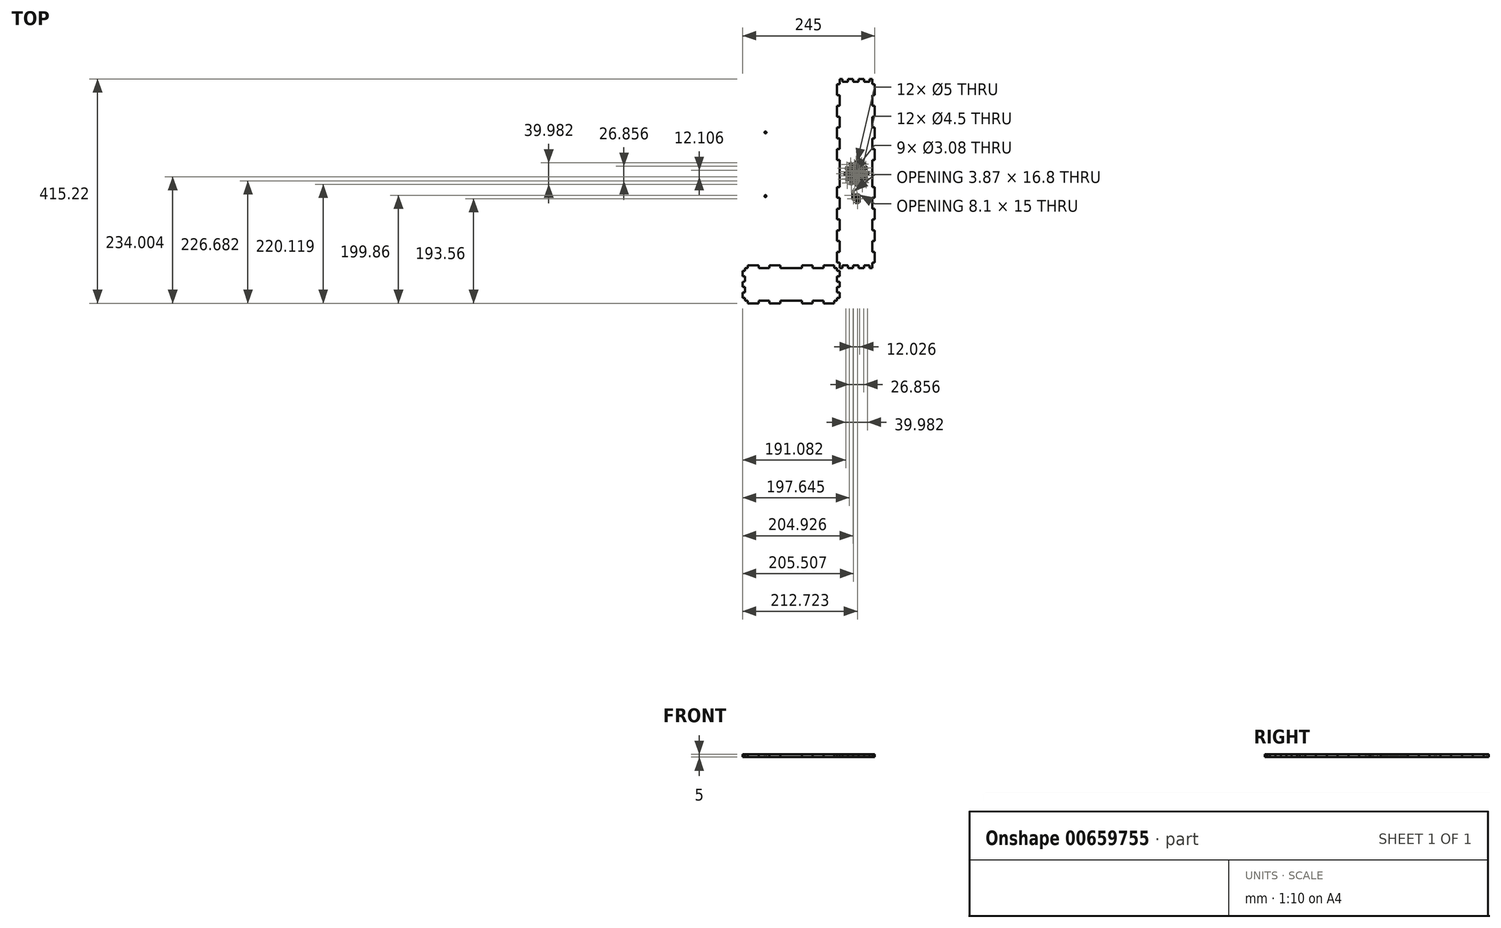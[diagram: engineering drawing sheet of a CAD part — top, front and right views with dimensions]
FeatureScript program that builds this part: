
annotation { "Feature Type Name" : "Feature", "Feature Type Description" : "" }
export const myFeature = defineFeature(function(context is Context, id is Id, definition is map)
    precondition{}
    {
        {
            assignVariable(context, id + "F0", {"name" : "thickness", "anyValue" : 5});
        }
        {
            var Q0;
            Q0=qCreatedBy(makeId("Top.planeOp"),FACE);
            var sketch = newSketch(context, id + "F1", { "sketchPlane" : qUnion([Q0])});
            skLineSegment(sketch, "E0", {"start": v(-90, 175.1) * mm, "end": v(-90, 165.1) * mm});
            skLineSegment(sketch, "E1", {"start": v(-80, 175.1) * mm, "end": v(-90, 175.1) * mm});
            skLineSegment(sketch, "E2", {"start": v(-80, 175.1) * mm, "end": v(-80, 170.1) * mm});
            skLineSegment(sketch, "E3", {"start": v(-80, 170.1) * mm, "end": v(-60, 170.1) * mm});
            skLineSegment(sketch, "E4", {"start": v(-60, 170.1) * mm, "end": v(-60, 175.1) * mm});
            skLineSegment(sketch, "E5.direction1", {"start": v(-80, 170.1) * mm, "end": v(-40, 170.1) * mm, "construction": true});
            skLineSegment(sketch, "E6", {"start": v(-90, 165.1) * mm, "end": v(-85, 165.1) * mm});
            skLineSegment(sketch, "E7", {"start": v(-85, 165.1) * mm, "end": v(-85, 145.1) * mm});
            skLineSegment(sketch, "E8", {"start": v(-85, 145.1) * mm, "end": v(-90, 145.1) * mm});
            skLineSegment(sketch, "E9.0.1.0", {"start": v(-90, 125.1) * mm, "end": v(-85, 125.1) * mm});
            skLineSegment(sketch, "E9.0.1.1", {"start": v(-85, 125.1) * mm, "end": v(-85, 105.1) * mm});
            skLineSegment(sketch, "E9.0.1.2", {"start": v(-85, 105.1) * mm, "end": v(-90, 105.1) * mm});
            skLineSegment(sketch, "E9.0.2.0", {"start": v(-90, 85.1) * mm, "end": v(-85, 85.1) * mm});
            skLineSegment(sketch, "E9.0.2.1", {"start": v(-85, 85.1) * mm, "end": v(-85, 65.1) * mm});
            skLineSegment(sketch, "E9.0.2.2", {"start": v(-85, 65.1) * mm, "end": v(-90, 65.1) * mm});
            skLineSegment(sketch, "E9.0.3.0", {"start": v(-90, 45.1) * mm, "end": v(-85, 45.1) * mm});
            skLineSegment(sketch, "E9.0.3.1", {"start": v(-85, 45.1) * mm, "end": v(-85, 25.1) * mm});
            skLineSegment(sketch, "E9.0.3.2", {"start": v(-85, 25.1) * mm, "end": v(-90, 25.1) * mm});
            skLineSegment(sketch, "E9.direction1", {"start": v(-90, 165.1) * mm, "end": v(-88.53, 165.1) * mm, "construction": true});
            skLineSegment(sketch, "E9.direction2", {"start": v(-90, 165.1) * mm, "end": v(-90, 125.1) * mm, "construction": true});
            skLineSegment(sketch, "E10.0.1.0", {"start": v(-40, 175.1) * mm, "end": v(-40, 170.1) * mm});
            skLineSegment(sketch, "E10.3.1.0", {"start": v(-40, 170.1) * mm, "end": v(-20, 170.1) * mm});
            skLineSegment(sketch, "E10.6.1.0", {"start": v(-20, 170.1) * mm, "end": v(-20, 175.1) * mm});
            skLineSegment(sketch, "E11", {"start": v(-60, 175.1) * mm, "end": v(-40, 175.1) * mm});
            skLineSegment(sketch, "E12", {"start": v(-20, 175.1) * mm, "end": v(0, 175.1) * mm});
            skLineSegment(sketch, "E13", {"start": v(-90, 145.1) * mm, "end": v(-90, 125.1) * mm});
            skLineSegment(sketch, "E14", {"start": v(-90, 105.1) * mm, "end": v(-90, 85.1) * mm});
            skLineSegment(sketch, "E15", {"start": v(-90, 65.1) * mm, "end": v(-90, 45.1) * mm});
            skLineSegment(sketch, "E16", {"start": v(-90, 25.1) * mm, "end": v(-90, 0) * mm});
            skLineSegment(sketch, "E17.MirrorCS", {"start": v(20, 175.1) * mm, "end": v(0, 175.1) * mm});
            skLineSegment(sketch, "E18.MirrorCS", {"start": v(20, 170.1) * mm, "end": v(20, 175.1) * mm});
            skLineSegment(sketch, "E19.MirrorCS", {"start": v(40, 170.1) * mm, "end": v(20, 170.1) * mm});
            skLineSegment(sketch, "E20.MirrorCS", {"start": v(40, 175.1) * mm, "end": v(40, 170.1) * mm});
            skLineSegment(sketch, "E21.MirrorCS", {"start": v(60, 175.1) * mm, "end": v(40, 175.1) * mm});
            skLineSegment(sketch, "E22.MirrorCS", {"start": v(60, 170.1) * mm, "end": v(60, 175.1) * mm});
            skLineSegment(sketch, "E23.MirrorCS", {"start": v(80, 170.1) * mm, "end": v(40, 170.1) * mm, "construction": true});
            skLineSegment(sketch, "E24.MirrorCS", {"start": v(80, 175.1) * mm, "end": v(80, 170.1) * mm});
            skLineSegment(sketch, "E25.MirrorCS", {"start": v(80, 175.1) * mm, "end": v(90, 175.1) * mm});
            skLineSegment(sketch, "E26.MirrorCS", {"start": v(90, 175.1) * mm, "end": v(90, 165.1) * mm});
            skLineSegment(sketch, "E27.MirrorCS", {"start": v(90, 165.1) * mm, "end": v(88.53, 165.1) * mm, "construction": true});
            skLineSegment(sketch, "E28.MirrorCS", {"start": v(85, 165.1) * mm, "end": v(85, 145.1) * mm});
            skLineSegment(sketch, "E29.MirrorCS", {"start": v(85, 145.1) * mm, "end": v(90, 145.1) * mm});
            skLineSegment(sketch, "E30.MirrorCS", {"start": v(90, 165.1) * mm, "end": v(90, 125.1) * mm, "construction": true});
            skLineSegment(sketch, "E31.MirrorCS", {"start": v(85, 125.1) * mm, "end": v(85, 105.1) * mm});
            skLineSegment(sketch, "E32.MirrorCS", {"start": v(90, 125.1) * mm, "end": v(85, 125.1) * mm});
            skLineSegment(sketch, "E33.MirrorCS", {"start": v(85, 105.1) * mm, "end": v(90, 105.1) * mm});
            skLineSegment(sketch, "E34.MirrorCS", {"start": v(85, 85.1) * mm, "end": v(85, 65.1) * mm});
            skLineSegment(sketch, "E35.MirrorCS", {"start": v(90, 105.1) * mm, "end": v(90, 85.1) * mm});
            skLineSegment(sketch, "E36.MirrorCS", {"start": v(90, 85.1) * mm, "end": v(85, 85.1) * mm});
            skLineSegment(sketch, "E37.MirrorCS", {"start": v(85, 65.1) * mm, "end": v(90, 65.1) * mm});
            skLineSegment(sketch, "E38.MirrorCS", {"start": v(90, 65.1) * mm, "end": v(90, 45.1) * mm});
            skLineSegment(sketch, "E39.MirrorCS", {"start": v(90, 45.1) * mm, "end": v(85, 45.1) * mm});
            skLineSegment(sketch, "E40.MirrorCS", {"start": v(85, 45.1) * mm, "end": v(85, 25.1) * mm});
            skLineSegment(sketch, "E41.MirrorCS", {"start": v(85, 25.1) * mm, "end": v(90, 25.1) * mm});
            skLineSegment(sketch, "E42.MirrorCS", {"start": v(90, 25.1) * mm, "end": v(90, 0) * mm});
            skLineSegment(sketch, "E43.MirrorCS", {"start": v(90, 165.1) * mm, "end": v(85, 165.1) * mm});
            skLineSegment(sketch, "E44.MirrorCS", {"start": v(90, 145.1) * mm, "end": v(90, 125.1) * mm});
            skLineSegment(sketch, "E45.MirrorCS", {"start": v(90, -165.1) * mm, "end": v(88.53, -165.1) * mm, "construction": true});
            skLineSegment(sketch, "E46.MirrorCS", {"start": v(90, -125.1) * mm, "end": v(85, -125.1) * mm});
            skLineSegment(sketch, "E47.MirrorCS", {"start": v(60, -170.1) * mm, "end": v(60, -175.1) * mm});
            skLineSegment(sketch, "E48.MirrorCS", {"start": v(90, -85.1) * mm, "end": v(85, -85.1) * mm});
            skLineSegment(sketch, "E49.MirrorCS", {"start": v(90, -175.1) * mm, "end": v(90, -165.1) * mm});
            skLineSegment(sketch, "E50.MirrorCS", {"start": v(85, -105.1) * mm, "end": v(90, -105.1) * mm});
            skLineSegment(sketch, "E51.MirrorCS", {"start": v(85, -145.1) * mm, "end": v(90, -145.1) * mm});
            skLineSegment(sketch, "E52.MirrorCS", {"start": v(85, -65.1) * mm, "end": v(90, -65.1) * mm});
            skLineSegment(sketch, "E53.MirrorCS", {"start": v(40, -175.1) * mm, "end": v(40, -170.1) * mm});
            skLineSegment(sketch, "E54.MirrorCS", {"start": v(80, -175.1) * mm, "end": v(80, -170.1) * mm});
            skLineSegment(sketch, "E55.MirrorCS", {"start": v(90, -145.1) * mm, "end": v(90, -125.1) * mm});
            skLineSegment(sketch, "E56.MirrorCS", {"start": v(20, -170.1) * mm, "end": v(20, -175.1) * mm});
            skLineSegment(sketch, "E57.MirrorCS", {"start": v(90, -45.1) * mm, "end": v(85, -45.1) * mm});
            skLineSegment(sketch, "E58.MirrorCS", {"start": v(90, -165.1) * mm, "end": v(85, -165.1) * mm});
            skLineSegment(sketch, "E59.MirrorCS", {"start": v(85, -25.1) * mm, "end": v(90, -25.1) * mm});
            skLineSegment(sketch, "E60.MirrorCS", {"start": v(90, -165.1) * mm, "end": v(90, -125.1) * mm, "construction": true});
            skLineSegment(sketch, "E61.MirrorCS", {"start": v(85, -125.1) * mm, "end": v(85, -105.1) * mm});
            skLineSegment(sketch, "E62.MirrorCS", {"start": v(40, -170.1) * mm, "end": v(20, -170.1) * mm});
            skLineSegment(sketch, "E63.MirrorCS", {"start": v(85, -45.1) * mm, "end": v(85, -25.1) * mm});
            skLineSegment(sketch, "E64.MirrorCS", {"start": v(80, -170.1) * mm, "end": v(40, -170.1) * mm, "construction": true});
            skLineSegment(sketch, "E65.MirrorCS", {"start": v(85, -85.1) * mm, "end": v(85, -65.1) * mm});
            skLineSegment(sketch, "E66.MirrorCS", {"start": v(20, -175.1) * mm, "end": v(0, -175.1) * mm});
            skLineSegment(sketch, "E67.MirrorCS", {"start": v(90, -65.1) * mm, "end": v(90, -45.1) * mm});
            skLineSegment(sketch, "E68.MirrorCS", {"start": v(80, -175.1) * mm, "end": v(85, -175.1) * mm});
            skLineSegment(sketch, "E69.MirrorCS", {"start": v(90, -105.1) * mm, "end": v(90, -85.1) * mm});
            skLineSegment(sketch, "E70.MirrorCS", {"start": v(90, -25.1) * mm, "end": v(90, 0) * mm});
            skLineSegment(sketch, "E71.MirrorCS", {"start": v(85, -165.1) * mm, "end": v(85, -145.1) * mm});
            skLineSegment(sketch, "E72.MirrorCS", {"start": v(60, -175.1) * mm, "end": v(40, -175.1) * mm});
            skLineSegment(sketch, "E73.MirrorCS", {"start": v(-90, -165.1) * mm, "end": v(-88.53, -165.1) * mm, "construction": true});
            skLineSegment(sketch, "E74.MirrorCS", {"start": v(-90, -165.1) * mm, "end": v(-85, -165.1) * mm});
            skLineSegment(sketch, "E75.MirrorCS", {"start": v(-90, -125.1) * mm, "end": v(-85, -125.1) * mm});
            skLineSegment(sketch, "E76.MirrorCS", {"start": v(-85, -105.1) * mm, "end": v(-90, -105.1) * mm});
            skLineSegment(sketch, "E77.MirrorCS", {"start": v(-40, -175.1) * mm, "end": v(-40, -170.1) * mm});
            skLineSegment(sketch, "E78.MirrorCS", {"start": v(-60, -170.1) * mm, "end": v(-60, -175.1) * mm});
            skLineSegment(sketch, "E79.MirrorCS", {"start": v(-85, -145.1) * mm, "end": v(-90, -145.1) * mm});
            skLineSegment(sketch, "E80.MirrorCS", {"start": v(-80, -175.1) * mm, "end": v(-80, -170.1) * mm});
            skLineSegment(sketch, "E81.MirrorCS", {"start": v(-85, -25.1) * mm, "end": v(-90, -25.1) * mm});
            skLineSegment(sketch, "E82.MirrorCS", {"start": v(-90, -45.1) * mm, "end": v(-85, -45.1) * mm});
            skLineSegment(sketch, "E83.MirrorCS", {"start": v(-90, -145.1) * mm, "end": v(-90, -125.1) * mm});
            skLineSegment(sketch, "E84.MirrorCS", {"start": v(-90, -85.1) * mm, "end": v(-85, -85.1) * mm});
            skLineSegment(sketch, "E85.MirrorCS", {"start": v(-20, -170.1) * mm, "end": v(-20, -175.1) * mm});
            skLineSegment(sketch, "E86.MirrorCS", {"start": v(-85, -65.1) * mm, "end": v(-90, -65.1) * mm});
            skLineSegment(sketch, "E87.MirrorCS", {"start": v(-80, -175.1) * mm, "end": v(-90, -175.1) * mm});
            skLineSegment(sketch, "E88.MirrorCS", {"start": v(-90, -175.1) * mm, "end": v(-90, -165.1) * mm});
            skLineSegment(sketch, "E89.MirrorCS", {"start": v(-90, -165.1) * mm, "end": v(-90, -125.1) * mm, "construction": true});
            skLineSegment(sketch, "E90.MirrorCS", {"start": v(-85, -125.1) * mm, "end": v(-85, -105.1) * mm});
            skLineSegment(sketch, "E91.MirrorCS", {"start": v(-85, -45.1) * mm, "end": v(-85, -25.1) * mm});
            skLineSegment(sketch, "E92.MirrorCS", {"start": v(-90, -65.1) * mm, "end": v(-90, -45.1) * mm});
            skLineSegment(sketch, "E93.MirrorCS", {"start": v(-90, -25.1) * mm, "end": v(-90, 0) * mm});
            skLineSegment(sketch, "E94.MirrorCS", {"start": v(-40, -170.1) * mm, "end": v(-20, -170.1) * mm});
            skLineSegment(sketch, "E95.MirrorCS", {"start": v(-20, -175.1) * mm, "end": v(0, -175.1) * mm});
            skLineSegment(sketch, "E96.MirrorCS", {"start": v(-90, -105.1) * mm, "end": v(-90, -85.1) * mm});
            skLineSegment(sketch, "E97.MirrorCS", {"start": v(-85, -165.1) * mm, "end": v(-85, -145.1) * mm});
            skLineSegment(sketch, "E98.MirrorCS", {"start": v(-80, -170.1) * mm, "end": v(-40, -170.1) * mm, "construction": true});
            skLineSegment(sketch, "E99.MirrorCS", {"start": v(-60, -175.1) * mm, "end": v(-40, -175.1) * mm});
            skLineSegment(sketch, "E100.MirrorCS", {"start": v(-85, -85.1) * mm, "end": v(-85, -65.1) * mm});
            skLineSegment(sketch, "E101", {"start": v(-80, -170.1) * mm, "end": v(-60, -170.1) * mm});
            skLineSegment(sketch, "E102", {"start": v(60, -170.1) * mm, "end": v(80, -170.1) * mm});
            skLineSegment(sketch, "E103", {"start": v(60, 170.1) * mm, "end": v(80, 170.1) * mm});
            skLineSegment(sketch, "E104", {"start": v(-95.98, -205.1) * mm, "end": v(120.4, -205.1) * mm, "construction": true});
            skLineSegment(sketch, "E105", {"start": v(-90, -180.1) * mm, "end": v(-90, -190.1) * mm});
            skLineSegment(sketch, "E106.MirrorCS", {"start": v(155, 165.1) * mm, "end": v(155, 145.1) * mm});
            skLineSegment(sketch, "E107", {"start": v(90, -175.1) * mm, "end": v(95, -175.1) * mm});
            skLineSegment(sketch, "E108", {"start": v(90, 175.1) * mm, "end": v(95, 175.1) * mm});
            skLineSegment(sketch, "E109", {"start": v(105, -175.1) * mm, "end": v(115, -175.1) * mm});
            skLineSegment(sketch, "E110", {"start": v(90, -180.1) * mm, "end": v(85, -180.1) * mm});
            skLineSegment(sketch, "E111", {"start": v(85, -190.1) * mm, "end": v(90, -190.1) * mm});
            skLineSegment(sketch, "E112", {"start": v(90, -180.1) * mm, "end": v(90, -190.1) * mm});
            skLineSegment(sketch, "E113", {"start": v(85, -175.1) * mm, "end": v(90, -175.1) * mm});
            skLineSegment(sketch, "E114", {"start": v(85, -175.1) * mm, "end": v(85, -180.1) * mm});
            skLineSegment(sketch, "E115", {"start": v(85, -190.1) * mm, "end": v(85, -200.1) * mm});
            skLineSegment(sketch, "E116", {"start": v(95, -175.1) * mm, "end": v(95, -170.1) * mm});
            skLineSegment(sketch, "E117", {"start": v(95, -170.1) * mm, "end": v(105, -170.1) * mm});
            skLineSegment(sketch, "E118", {"start": v(105, -170.1) * mm, "end": v(105, -175.1) * mm});
            skLineSegment(sketch, "E119", {"start": v(125, -175.1) * mm, "end": v(125, -170.1) * mm});
            skLineSegment(sketch, "E120", {"start": v(125, -170.1) * mm, "end": v(115, -170.1) * mm});
            skLineSegment(sketch, "E121", {"start": v(115, -170.1) * mm, "end": v(115, -175.1) * mm});
            skLineSegment(sketch, "E122.MirrorCS", {"start": v(-85, -175.1) * mm, "end": v(-85, -180.1) * mm});
            skLineSegment(sketch, "E123.MirrorCS", {"start": v(-90, -180.1) * mm, "end": v(-85, -180.1) * mm});
            skLineSegment(sketch, "E124.MirrorCS", {"start": v(-85, -190.1) * mm, "end": v(-90, -190.1) * mm});
            skLineSegment(sketch, "E125.MirrorCS", {"start": v(-85, -190.1) * mm, "end": v(-85, -200.1) * mm});
            skLineSegment(sketch, "E126.MirrorCS", {"start": v(95, 175.1) * mm, "end": v(95, 170.1) * mm});
            skLineSegment(sketch, "E127.MirrorCS", {"start": v(95, 170.1) * mm, "end": v(105, 170.1) * mm});
            skLineSegment(sketch, "E128.MirrorCS", {"start": v(105, 170.1) * mm, "end": v(105, 175.1) * mm});
            skLineSegment(sketch, "E129.MirrorCS", {"start": v(105, 175.1) * mm, "end": v(115, 175.1) * mm});
            skLineSegment(sketch, "E130.MirrorCS", {"start": v(115, 170.1) * mm, "end": v(115, 175.1) * mm});
            skArc(sketch, "E131", {"start": v(114.77, -46.85) * mm, "mid": v(114.95, -47.27) * mm, "end": v(115.37, -47.45) * mm});
            skArc(sketch, "E132", {"start": v(117.47, -40.25) * mm, "mid": v(117.05, -40.43) * mm, "end": v(116.87, -40.85) * mm});
            skArc(sketch, "E133", {"start": v(119.27, -44.49) * mm, "mid": v(119.37, -44.74) * mm, "end": v(119.62, -44.85) * mm});
            skLineSegment(sketch, "E134", {"start": v(122.87, -47.45) * mm, "end": v(122.3, -47.45) * mm});
            skArc(sketch, "E135", {"start": v(122.87, -47.45) * mm, "mid": v(123.3, -47.27) * mm, "end": v(123.47, -46.85) * mm});
            skLineSegment(sketch, "E136", {"start": v(117.47, -40.25) * mm, "end": v(118.38, -40.25) * mm});
            skArc(sketch, "E137", {"start": v(125.57, -40.85) * mm, "mid": v(125.4, -40.43) * mm, "end": v(124.97, -40.25) * mm});
            skLineSegment(sketch, "E138", {"start": v(125.57, -40.85) * mm, "end": v(125.57, -52.25) * mm});
            skArc(sketch, "E139", {"start": v(124.97, -52.85) * mm, "mid": v(125.4, -52.67) * mm, "end": v(125.57, -52.25) * mm});
            skLineSegment(sketch, "E140", {"start": v(121.07, -44.5) * mm, "end": v(121.07, -43) * mm});
            skArc(sketch, "E141", {"start": v(121.07, -43) * mm, "mid": v(121.03, -42.9) * mm, "end": v(120.92, -42.85) * mm});
            skLineSegment(sketch, "E142", {"start": v(122.27, -43) * mm, "end": v(122.27, -44.5) * mm});
            skArc(sketch, "E143", {"start": v(122.27, -43) * mm, "mid": v(121.88, -42.05) * mm, "end": v(120.92, -41.65) * mm});
            skLineSegment(sketch, "E144", {"start": v(118.07, -44.5) * mm, "end": v(118.07, -43.3) * mm});
            skArc(sketch, "E145", {"start": v(118.07, -44.5) * mm, "mid": v(118.53, -45.6) * mm, "end": v(119.62, -46.05) * mm});
            skArc(sketch, "E146", {"start": v(117.47, -39.05) * mm, "mid": v(116.2, -39.58) * mm, "end": v(115.67, -40.85) * mm});
            skLineSegment(sketch, "E147", {"start": v(124.97, -39.05) * mm, "end": v(123.59, -39.05) * mm});
            skArc(sketch, "E148", {"start": v(126.77, -40.85) * mm, "mid": v(126.25, -39.58) * mm, "end": v(124.97, -39.05) * mm});
            skArc(sketch, "E149", {"start": v(122.87, -48.65) * mm, "mid": v(124.15, -48.12) * mm, "end": v(124.67, -46.85) * mm});
            skLineSegment(sketch, "E150", {"start": v(126.77, -52.25) * mm, "end": v(126.77, -40.85) * mm});
            skArc(sketch, "E151", {"start": v(124.97, -54.05) * mm, "mid": v(126.25, -53.52) * mm, "end": v(126.77, -52.25) * mm});
            skLineSegment(sketch, "E152", {"start": v(122.87, -48.65) * mm, "end": v(122.3, -48.65) * mm});
            skArc(sketch, "E153", {"start": v(113.57, -46.85) * mm, "mid": v(114.1, -48.12) * mm, "end": v(115.37, -48.65) * mm});
            skLineSegment(sketch, "E154", {"start": v(114.77, -46.85) * mm, "end": v(114.77, -31.85) * mm});
            skLineSegment(sketch, "E155", {"start": v(115.67, -46.05) * mm, "end": v(115.67, -40.85) * mm});
            skLineSegment(sketch, "E156", {"start": v(116.87, -46.05) * mm, "end": v(116.87, -40.85) * mm});
            skLineSegment(sketch, "E157", {"start": v(116.87, -46.05) * mm, "end": v(115.67, -46.05) * mm});
            skLineSegment(sketch, "E158", {"start": v(120.92, -42.85) * mm, "end": v(118.07, -42.85) * mm});
            skLineSegment(sketch, "E159", {"start": v(118.07, -42.85) * mm, "end": v(118.07, -41.65) * mm});
            skLineSegment(sketch, "E160", {"start": v(118.07, -41.65) * mm, "end": v(120.92, -41.65) * mm});
            skLineSegment(sketch, "E161", {"start": v(122.27, -46.05) * mm, "end": v(119.62, -46.05) * mm});
            skLineSegment(sketch, "E162", {"start": v(122.27, -44.85) * mm, "end": v(122.27, -46.05) * mm});
            skLineSegment(sketch, "E163", {"start": v(119.62, -44.85) * mm, "end": v(122.27, -44.85) * mm});
            skLineSegment(sketch, "E164", {"start": v(123.47, -41.65) * mm, "end": v(123.47, -46.85) * mm});
            skLineSegment(sketch, "E165", {"start": v(124.67, -41.65) * mm, "end": v(123.47, -41.65) * mm});
            skLineSegment(sketch, "E166", {"start": v(124.67, -41.65) * mm, "end": v(124.67, -46.85) * mm});
            skLineSegment(sketch, "E167", {"start": v(124.97, -52.85) * mm, "end": v(118.67, -52.85) * mm});
            skLineSegment(sketch, "E168", {"start": v(118.67, -52.85) * mm, "end": v(118.67, -54.05) * mm});
            skLineSegment(sketch, "E169", {"start": v(118.67, -54.05) * mm, "end": v(124.97, -54.05) * mm});
            skLineSegment(sketch, "E170", {"start": v(121.07, -44.5) * mm, "end": v(122.27, -44.5) * mm});
            skLineSegment(sketch, "E171", {"start": v(118.07, -43.3) * mm, "end": v(119.27, -43.3) * mm});
            skLineSegment(sketch, "E172", {"start": v(113.57, -46.85) * mm, "end": v(113.57, -31.85) * mm});
            skLineSegment(sketch, "E173", {"start": v(113.57, -31.85) * mm, "end": v(114.77, -31.85) * mm});
            skLineSegment(sketch, "E174", {"start": v(114.17, -34.59) * mm, "end": v(114.17, -46.85) * mm, "construction": true});
            skLineSegment(sketch, "E175", {"start": v(116.27, -46.4) * mm, "end": v(116.27, -40.85) * mm, "construction": true});
            skLineSegment(sketch, "E176", {"start": v(124.07, -42.42) * mm, "end": v(124.07, -46.85) * mm, "construction": true});
            skLineSegment(sketch, "E177", {"start": v(122.47, -45.45) * mm, "end": v(119.62, -45.45) * mm, "construction": true});
            skLineSegment(sketch, "E178", {"start": v(121.67, -45.3) * mm, "end": v(121.67, -43) * mm, "construction": true});
            skLineSegment(sketch, "E179", {"start": v(118.46, -42.25) * mm, "end": v(120.92, -42.25) * mm, "construction": true});
            skLineSegment(sketch, "E180", {"start": v(117.48, -53.45) * mm, "end": v(124.97, -53.45) * mm, "construction": true});
            skLineSegment(sketch, "E181", {"start": v(117.47, -39.65) * mm, "end": v(124.97, -39.65) * mm, "construction": true});
            skLineSegment(sketch, "E182", {"start": v(118.67, -43.97) * mm, "end": v(118.67, -44.5) * mm, "construction": true});
            skLineSegment(sketch, "E183", {"start": v(122.87, -48.05) * mm, "end": v(115.37, -48.05) * mm, "construction": true});
            skLineSegment(sketch, "E184", {"start": v(126.17, -40.85) * mm, "end": v(126.17, -52.25) * mm, "construction": true});
            skArc(sketch, "E185.filletArc", {"start": v(121.67, -43) * mm, "mid": v(121.45, -42.47) * mm, "end": v(120.92, -42.25) * mm, "construction": true});
            skArc(sketch, "E186.filletArc", {"start": v(118.67, -44.5) * mm, "mid": v(118.95, -45.17) * mm, "end": v(119.62, -45.45) * mm, "construction": true});
            skArc(sketch, "E187.filletArc", {"start": v(117.47, -39.65) * mm, "mid": v(116.62, -40) * mm, "end": v(116.27, -40.85) * mm, "construction": true});
            skArc(sketch, "E188.filletArc", {"start": v(126.17, -40.85) * mm, "mid": v(125.82, -40) * mm, "end": v(124.97, -39.65) * mm, "construction": true});
            skArc(sketch, "E189.filletArc", {"start": v(122.87, -48.05) * mm, "mid": v(123.72, -47.7) * mm, "end": v(124.07, -46.85) * mm, "construction": true});
            skArc(sketch, "E190.filletArc", {"start": v(124.97, -53.45) * mm, "mid": v(125.82, -53.1) * mm, "end": v(126.17, -52.25) * mm, "construction": true});
            skArc(sketch, "E191.filletArc", {"start": v(114.17, -46.85) * mm, "mid": v(114.52, -47.7) * mm, "end": v(115.37, -48.05) * mm, "construction": true});
            skLineSegment(sketch, "E192", {"start": v(128.05, -43.85) * mm, "end": v(111.92, -43.85) * mm, "construction": true});
            skLineSegment(sketch, "E193", {"start": v(120.17, -39.21) * mm, "end": v(120.17, -54.4) * mm, "construction": true});
            skLineSegment(sketch, "E194", {"start": v(117.44, -47.45) * mm, "end": v(117.44, -48.65) * mm});
            skLineSegment(sketch, "E195", {"start": v(117.7, -47.45) * mm, "end": v(117.7, -48.65) * mm});
            skLineSegment(sketch, "E196.trimOffspring", {"start": v(117.44, -47.45) * mm, "end": v(115.37, -47.45) * mm});
            skLineSegment(sketch, "E197.trimOffspring", {"start": v(117.44, -48.65) * mm, "end": v(115.37, -48.65) * mm});
            skLineSegment(sketch, "E198", {"start": v(122.3, -47.45) * mm, "end": v(122.3, -48.65) * mm});
            skLineSegment(sketch, "E199", {"start": v(122.06, -47.45) * mm, "end": v(122.06, -48.65) * mm});
            skLineSegment(sketch, "E200.trimOffspring", {"start": v(122.06, -47.45) * mm, "end": v(117.7, -47.45) * mm});
            skLineSegment(sketch, "E201.trimOffspring", {"start": v(122.06, -48.65) * mm, "end": v(117.7, -48.65) * mm});
            skLineSegment(sketch, "E202", {"start": v(123.59, -39.05) * mm, "end": v(123.59, -40.25) * mm});
            skLineSegment(sketch, "E203", {"start": v(123.34, -39.05) * mm, "end": v(123.34, -40.25) * mm});
            skLineSegment(sketch, "E204", {"start": v(118.38, -39.05) * mm, "end": v(118.38, -40.25) * mm});
            skLineSegment(sketch, "E205", {"start": v(118.63, -39.05) * mm, "end": v(118.63, -40.25) * mm});
            skLineSegment(sketch, "E206.trimOffspring", {"start": v(118.38, -39.05) * mm, "end": v(117.47, -39.05) * mm});
            skLineSegment(sketch, "E207.trimOffspring", {"start": v(118.63, -40.25) * mm, "end": v(123.34, -40.25) * mm});
            skLineSegment(sketch, "E208.trimOffspring", {"start": v(123.34, -39.05) * mm, "end": v(118.63, -39.05) * mm});
            skLineSegment(sketch, "E209.trimOffspring", {"start": v(123.59, -40.25) * mm, "end": v(124.97, -40.25) * mm});
            skLineSegment(sketch, "E210", {"start": v(119.27, -44.49) * mm, "end": v(119.27, -43.3) * mm});
            skLineSegment(sketch, "E211", {"start": v(120, 16.73) * mm, "end": v(120, -85.19) * mm, "construction": true});
            skLineSegment(sketch, "E212.MirrorCS", {"start": v(150, 125.1) * mm, "end": v(155, 125.1) * mm});
            skLineSegment(sketch, "E213.MirrorCS", {"start": v(150, 145.1) * mm, "end": v(150, 125.1) * mm});
            skLineSegment(sketch, "E214.MirrorCS", {"start": v(150, 45.1) * mm, "end": v(155, 45.1) * mm});
            skLineSegment(sketch, "E215.MirrorCS", {"start": v(155, 145.1) * mm, "end": v(150, 145.1) * mm});
            skLineSegment(sketch, "E216.MirrorCS", {"start": v(155, 105.1) * mm, "end": v(150, 105.1) * mm});
            skLineSegment(sketch, "E217.MirrorCS", {"start": v(155, 25.1) * mm, "end": v(150, 25.1) * mm});
            skLineSegment(sketch, "E218.MirrorCS", {"start": v(150, 85.1) * mm, "end": v(155, 85.1) * mm});
            skLineSegment(sketch, "E219.MirrorCS", {"start": v(155, 65.1) * mm, "end": v(150, 65.1) * mm});
            skLineSegment(sketch, "E220.MirrorCS", {"start": v(155, 125.1) * mm, "end": v(155, 105.1) * mm});
            skLineSegment(sketch, "E221.MirrorCS", {"start": v(150, 165.1) * mm, "end": v(150, 125.1) * mm, "construction": true});
            skLineSegment(sketch, "E222.MirrorCS", {"start": v(155, 85.1) * mm, "end": v(155, 65.1) * mm});
            skLineSegment(sketch, "E223.MirrorCS", {"start": v(150, 105.1) * mm, "end": v(150, 85.1) * mm});
            skLineSegment(sketch, "E224.MirrorCS", {"start": v(150, 25.1) * mm, "end": v(150, 0) * mm});
            skLineSegment(sketch, "E225.MirrorCS", {"start": v(155, 45.1) * mm, "end": v(155, 25.1) * mm});
            skLineSegment(sketch, "E226.MirrorCS", {"start": v(150, 65.1) * mm, "end": v(150, 45.1) * mm});
            skLineSegment(sketch, "E227.MirrorCS", {"start": v(150, 165.1) * mm, "end": v(155, 165.1) * mm});
            skLineSegment(sketch, "E228.MirrorCS", {"start": v(150, 175.1) * mm, "end": v(150, 165.1) * mm});
            skLineSegment(sketch, "E229.MirrorCS", {"start": v(145, 170.1) * mm, "end": v(135, 170.1) * mm});
            skLineSegment(sketch, "E230.MirrorCS", {"start": v(135, 170.1) * mm, "end": v(135, 175.1) * mm});
            skLineSegment(sketch, "E231.MirrorCS", {"start": v(145, 175.1) * mm, "end": v(145, 170.1) * mm});
            skLineSegment(sketch, "E232.MirrorCS", {"start": v(150, 175.1) * mm, "end": v(145, 175.1) * mm});
            skLineSegment(sketch, "E233.MirrorCS", {"start": v(135, 175.1) * mm, "end": v(125, 175.1) * mm});
            skLineSegment(sketch, "E234.MirrorCS", {"start": v(125, 170.1) * mm, "end": v(125, 175.1) * mm});
            skLineSegment(sketch, "E235.MirrorCS", {"start": v(150, -25.1) * mm, "end": v(150, 0) * mm});
            skLineSegment(sketch, "E236.MirrorCS", {"start": v(150, -45.1) * mm, "end": v(155, -45.1) * mm});
            skLineSegment(sketch, "E237.MirrorCS", {"start": v(155, -65.1) * mm, "end": v(150, -65.1) * mm});
            skLineSegment(sketch, "E238.MirrorCS", {"start": v(155, -45.1) * mm, "end": v(155, -25.1) * mm});
            skLineSegment(sketch, "E239.MirrorCS", {"start": v(155, -85.1) * mm, "end": v(155, -65.1) * mm});
            skLineSegment(sketch, "E240.MirrorCS", {"start": v(150, -85.1) * mm, "end": v(155, -85.1) * mm});
            skLineSegment(sketch, "E241.MirrorCS", {"start": v(155, -25.1) * mm, "end": v(150, -25.1) * mm});
            skLineSegment(sketch, "E242.MirrorCS", {"start": v(150, -105.1) * mm, "end": v(150, -85.1) * mm});
            skLineSegment(sketch, "E243.MirrorCS", {"start": v(150, -65.1) * mm, "end": v(150, -45.1) * mm});
            skLineSegment(sketch, "E244.MirrorCS", {"start": v(150, -165.1) * mm, "end": v(151.47, -165.1) * mm, "construction": true});
            skLineSegment(sketch, "E245.MirrorCS", {"start": v(150, -165.1) * mm, "end": v(155, -165.1) * mm});
            skLineSegment(sketch, "E246.MirrorCS", {"start": v(150, -145.1) * mm, "end": v(150, -125.1) * mm});
            skLineSegment(sketch, "E247.MirrorCS", {"start": v(155, -125.1) * mm, "end": v(155, -105.1) * mm});
            skLineSegment(sketch, "E248.MirrorCS", {"start": v(150, -165.1) * mm, "end": v(150, -125.1) * mm, "construction": true});
            skLineSegment(sketch, "E249.MirrorCS", {"start": v(150, -125.1) * mm, "end": v(155, -125.1) * mm});
            skLineSegment(sketch, "E250.MirrorCS", {"start": v(155, -165.1) * mm, "end": v(155, -145.1) * mm});
            skLineSegment(sketch, "E251.MirrorCS", {"start": v(155, -145.1) * mm, "end": v(150, -145.1) * mm});
            skLineSegment(sketch, "E252.MirrorCS", {"start": v(155, -105.1) * mm, "end": v(150, -105.1) * mm});
            skLineSegment(sketch, "E253.MirrorCS", {"start": v(150, -175.1) * mm, "end": v(150, -165.1) * mm});
            skLineSegment(sketch, "E254.MirrorCS", {"start": v(150, -175.1) * mm, "end": v(145, -175.1) * mm});
            skLineSegment(sketch, "E255.MirrorCS", {"start": v(145, -175.1) * mm, "end": v(145, -170.1) * mm});
            skLineSegment(sketch, "E256.MirrorCS", {"start": v(145, -170.1) * mm, "end": v(135, -170.1) * mm});
            skLineSegment(sketch, "E257.MirrorCS", {"start": v(135, -170.1) * mm, "end": v(135, -175.1) * mm});
            skLineSegment(sketch, "E258", {"start": v(125, -175.1) * mm, "end": v(135, -175.1) * mm});
            skLineSegment(sketch, "E259", {"start": v(115, 170.1) * mm, "end": v(125, 170.1) * mm});
            skLineSegment(sketch, "E260.MirrorCS", {"start": v(-80, -235.1) * mm, "end": v(-80, -240.1) * mm});
            skLineSegment(sketch, "E261.MirrorCS", {"start": v(-20, -240.1) * mm, "end": v(-20, -235.1) * mm});
            skLineSegment(sketch, "E262.MirrorCS", {"start": v(40, -235.1) * mm, "end": v(40, -240.1) * mm});
            skLineSegment(sketch, "E263.MirrorCS", {"start": v(20, -240.1) * mm, "end": v(20, -235.1) * mm});
            skLineSegment(sketch, "E264.MirrorCS", {"start": v(80, -235.1) * mm, "end": v(80, -240.1) * mm});
            skLineSegment(sketch, "E265.MirrorCS", {"start": v(-60, -240.1) * mm, "end": v(-60, -235.1) * mm});
            skLineSegment(sketch, "E266.MirrorCS", {"start": v(-40, -235.1) * mm, "end": v(-40, -240.1) * mm});
            skLineSegment(sketch, "E267.MirrorCS", {"start": v(60, -240.1) * mm, "end": v(60, -235.1) * mm});
            skLineSegment(sketch, "E268.MirrorCS", {"start": v(60, -240.1) * mm, "end": v(80, -240.1) * mm});
            skLineSegment(sketch, "E269.MirrorCS", {"start": v(-80, -240.1) * mm, "end": v(-60, -240.1) * mm});
            skLineSegment(sketch, "E270.MirrorCS", {"start": v(-60, -235.1) * mm, "end": v(-40, -235.1) * mm});
            skLineSegment(sketch, "E271.MirrorCS", {"start": v(20, -235.1) * mm, "end": v(0, -235.1) * mm});
            skLineSegment(sketch, "E272.MirrorCS", {"start": v(60, -235.1) * mm, "end": v(40, -235.1) * mm});
            skLineSegment(sketch, "E273.MirrorCS", {"start": v(-80, -240.1) * mm, "end": v(-40, -240.1) * mm, "construction": true});
            skLineSegment(sketch, "E274.MirrorCS", {"start": v(-20, -235.1) * mm, "end": v(0, -235.1) * mm});
            skLineSegment(sketch, "E275.MirrorCS", {"start": v(80, -240.1) * mm, "end": v(40, -240.1) * mm, "construction": true});
            skLineSegment(sketch, "E276.MirrorCS", {"start": v(40, -240.1) * mm, "end": v(20, -240.1) * mm});
            skLineSegment(sketch, "E277.MirrorCS", {"start": v(-40, -240.1) * mm, "end": v(-20, -240.1) * mm});
            skLineSegment(sketch, "E278.MirrorCS", {"start": v(-85, -235.1) * mm, "end": v(-85, -230.1) * mm});
            skLineSegment(sketch, "E279.MirrorCS", {"start": v(-85, -220.1) * mm, "end": v(-90, -220.1) * mm});
            skLineSegment(sketch, "E280.MirrorCS", {"start": v(-85, -220.1) * mm, "end": v(-85, -210.1) * mm});
            skLineSegment(sketch, "E281.MirrorCS", {"start": v(-90, -230.1) * mm, "end": v(-85, -230.1) * mm});
            skLineSegment(sketch, "E282.MirrorCS", {"start": v(-90, -230.1) * mm, "end": v(-90, -220.1) * mm});
            skLineSegment(sketch, "E283.MirrorCS", {"start": v(90, -230.1) * mm, "end": v(85, -230.1) * mm});
            skLineSegment(sketch, "E284.MirrorCS", {"start": v(85, -220.1) * mm, "end": v(90, -220.1) * mm});
            skLineSegment(sketch, "E285.MirrorCS", {"start": v(85, -220.1) * mm, "end": v(85, -210.1) * mm});
            skLineSegment(sketch, "E286.MirrorCS", {"start": v(90, -230.1) * mm, "end": v(90, -220.1) * mm});
            skLineSegment(sketch, "E287.MirrorCS", {"start": v(80, -235.1) * mm, "end": v(85, -235.1) * mm});
            skLineSegment(sketch, "E288.MirrorCS", {"start": v(85, -235.1) * mm, "end": v(85, -230.1) * mm});
            skLineSegment(sketch, "E289", {"start": v(-85, -235.1) * mm, "end": v(-80, -235.1) * mm});
            skLineSegment(sketch, "E290", {"start": v(-85, -210.1) * mm, "end": v(-90, -210.1) * mm});
            skLineSegment(sketch, "E291", {"start": v(-90, -210.1) * mm, "end": v(-90, -200.1) * mm});
            skLineSegment(sketch, "E292", {"start": v(-90, -200.1) * mm, "end": v(-84.99, -200.05) * mm});
            skLineSegment(sketch, "E293", {"start": v(85, -200.1) * mm, "end": v(90, -200.1) * mm});
            skLineSegment(sketch, "E294", {"start": v(90, -200.1) * mm, "end": v(90, -210.1) * mm});
            skLineSegment(sketch, "E295", {"start": v(90, -210.1) * mm, "end": v(85, -210.1) * mm});
            skSolve(sketch);
        }
        {
            var Q0;
            Q0=makeQuery(id+"F1.imprint","IMPRINT",FACE,{"disambiguationData":[TD([[makeQuery(id+"F1.imprint","IMPRINT",EDGE,{"derivedFrom":sQuery(id+"F1.wireOp",EDGE,"E0")}),1.0]])]});
            extrude(context, id + "F2", {"entities" : qUnion([Q0]), "depth" : (getVariable(context, 'thickness')) * mm, "offsetDistance" : 25 * mm});
        }
        {
            var Q0;
            Q0=makeQuery(id+"F1.imprint","IMPRINT",FACE,{"disambiguationData":[TD([[makeQuery(id+"F1.imprint","IMPRINT",EDGE,{"derivedFrom":sQuery(id+"F1.wireOp",EDGE,"E47.MirrorCS")}),1.0]])]});
            extrude(context, id + "F3", {"entities" : qUnion([Q0]), "depth" : (getVariable(context, 'thickness')) * mm, "offsetDistance" : 25 * mm});
        }
        {
            var Q0;
            Q0=makeQuery(id+"F1.imprint","IMPRINT",FACE,{"disambiguationData":[TD([[makeQuery(id+"F1.imprint","IMPRINT",EDGE,{"derivedFrom":sQuery(id+"F1.wireOp",EDGE,"E28.MirrorCS")}),1.0]])]});
            extrude(context, id + "F4", {"entities" : qUnion([Q0]), "depth" : (getVariable(context, 'thickness')) * mm, "offsetDistance" : 25 * mm});
        }
        {
            var Q0;
            Q0=makeQuery(id+"F2.opExtrude","CAP_FACE",FACE,{"disambiguationData":[OSD([sQuery(id+"F1.wireOp",EDGE,"E0"),sQuery(id+"F1.wireOp",EDGE,"E1"),sQuery(id+"F1.wireOp",EDGE,"E2"),sQuery(id+"F1.wireOp",EDGE,"E3"),sQuery(id+"F1.wireOp",EDGE,"E4"),sQuery(id+"F1.wireOp",EDGE,"E7"),sQuery(id+"F1.wireOp",EDGE,"E8"),sQuery(id+"F1.wireOp",EDGE,"E9.0.1.0"),sQuery(id+"F1.wireOp",EDGE,"E9.0.1.1"),sQuery(id+"F1.wireOp",EDGE,"E9.0.1.2"),sQuery(id+"F1.wireOp",EDGE,"E9.0.2.0"),sQuery(id+"F1.wireOp",EDGE,"E9.0.2.1"),sQuery(id+"F1.wireOp",EDGE,"E9.0.2.2"),sQuery(id+"F1.wireOp",EDGE,"E9.0.3.0"),sQuery(id+"F1.wireOp",EDGE,"E9.0.3.1"),sQuery(id+"F1.wireOp",EDGE,"E9.0.3.2"),sQuery(id+"F1.wireOp",EDGE,"E10.0.1.0"),sQuery(id+"F1.wireOp",EDGE,"E10.3.1.0"),sQuery(id+"F1.wireOp",EDGE,"E10.6.1.0"),sQuery(id+"F1.wireOp",EDGE,"E11"),sQuery(id+"F1.wireOp",EDGE,"E12"),sQuery(id+"F1.wireOp",EDGE,"E14"),sQuery(id+"F1.wireOp",EDGE,"E15"),sQuery(id+"F1.wireOp",EDGE,"E16"),sQuery(id+"F1.wireOp",EDGE,"E17.MirrorCS"),sQuery(id+"F1.wireOp",EDGE,"E18.MirrorCS"),sQuery(id+"F1.wireOp",EDGE,"E19.MirrorCS"),sQuery(id+"F1.wireOp",EDGE,"E20.MirrorCS"),sQuery(id+"F1.wireOp",EDGE,"E21.MirrorCS"),sQuery(id+"F1.wireOp",EDGE,"E22.MirrorCS"),sQuery(id+"F1.wireOp",EDGE,"E24.MirrorCS"),sQuery(id+"F1.wireOp",EDGE,"E25.MirrorCS"),sQuery(id+"F1.wireOp",EDGE,"E28.MirrorCS"),sQuery(id+"F1.wireOp",EDGE,"E29.MirrorCS"),sQuery(id+"F1.wireOp",EDGE,"E32.MirrorCS"),sQuery(id+"F1.wireOp",EDGE,"E31.MirrorCS"),sQuery(id+"F1.wireOp",EDGE,"E33.MirrorCS"),sQuery(id+"F1.wireOp",EDGE,"E34.MirrorCS"),sQuery(id+"F1.wireOp",EDGE,"E35.MirrorCS"),sQuery(id+"F1.wireOp",EDGE,"E36.MirrorCS"),sQuery(id+"F1.wireOp",EDGE,"E37.MirrorCS"),sQuery(id+"F1.wireOp",EDGE,"E38.MirrorCS"),sQuery(id+"F1.wireOp",EDGE,"E39.MirrorCS"),sQuery(id+"F1.wireOp",EDGE,"E40.MirrorCS"),sQuery(id+"F1.wireOp",EDGE,"E41.MirrorCS"),sQuery(id+"F1.wireOp",EDGE,"E42.MirrorCS"),sQuery(id+"F1.wireOp",EDGE,"E6"),sQuery(id+"F1.wireOp",EDGE,"E43.MirrorCS"),sQuery(id+"F1.wireOp",EDGE,"E13"),sQuery(id+"F1.wireOp",EDGE,"E44.MirrorCS"),sQuery(id+"F1.wireOp",EDGE,"E46.MirrorCS"),sQuery(id+"F1.wireOp",EDGE,"E47.MirrorCS"),sQuery(id+"F1.wireOp",EDGE,"E48.MirrorCS"),sQuery(id+"F1.wireOp",EDGE,"E49.MirrorCS"),sQuery(id+"F1.wireOp",EDGE,"E50.MirrorCS"),sQuery(id+"F1.wireOp",EDGE,"E51.MirrorCS"),sQuery(id+"F1.wireOp",EDGE,"E52.MirrorCS"),sQuery(id+"F1.wireOp",EDGE,"E53.MirrorCS"),sQuery(id+"F1.wireOp",EDGE,"E54.MirrorCS"),sQuery(id+"F1.wireOp",EDGE,"E55.MirrorCS"),sQuery(id+"F1.wireOp",EDGE,"E56.MirrorCS"),sQuery(id+"F1.wireOp",EDGE,"E57.MirrorCS"),sQuery(id+"F1.wireOp",EDGE,"E58.MirrorCS"),sQuery(id+"F1.wireOp",EDGE,"E59.MirrorCS"),sQuery(id+"F1.wireOp",EDGE,"E62.MirrorCS"),sQuery(id+"F1.wireOp",EDGE,"E63.MirrorCS"),sQuery(id+"F1.wireOp",EDGE,"E65.MirrorCS"),sQuery(id+"F1.wireOp",EDGE,"E66.MirrorCS"),sQuery(id+"F1.wireOp",EDGE,"E67.MirrorCS"),sQuery(id+"F1.wireOp",EDGE,"E68.MirrorCS"),sQuery(id+"F1.wireOp",EDGE,"E69.MirrorCS"),sQuery(id+"F1.wireOp",EDGE,"E70.MirrorCS"),sQuery(id+"F1.wireOp",EDGE,"E71.MirrorCS"),sQuery(id+"F1.wireOp",EDGE,"E72.MirrorCS"),sQuery(id+"F1.wireOp",EDGE,"E61.MirrorCS"),sQuery(id+"F1.wireOp",EDGE,"E74.MirrorCS"),sQuery(id+"F1.wireOp",EDGE,"E75.MirrorCS"),sQuery(id+"F1.wireOp",EDGE,"E76.MirrorCS"),sQuery(id+"F1.wireOp",EDGE,"E77.MirrorCS"),sQuery(id+"F1.wireOp",EDGE,"E78.MirrorCS"),sQuery(id+"F1.wireOp",EDGE,"E79.MirrorCS"),sQuery(id+"F1.wireOp",EDGE,"E80.MirrorCS"),sQuery(id+"F1.wireOp",EDGE,"E81.MirrorCS"),sQuery(id+"F1.wireOp",EDGE,"E82.MirrorCS"),sQuery(id+"F1.wireOp",EDGE,"E83.MirrorCS"),sQuery(id+"F1.wireOp",EDGE,"E84.MirrorCS"),sQuery(id+"F1.wireOp",EDGE,"E85.MirrorCS"),sQuery(id+"F1.wireOp",EDGE,"E86.MirrorCS"),sQuery(id+"F1.wireOp",EDGE,"E87.MirrorCS"),sQuery(id+"F1.wireOp",EDGE,"E88.MirrorCS"),sQuery(id+"F1.wireOp",EDGE,"E91.MirrorCS"),sQuery(id+"F1.wireOp",EDGE,"E92.MirrorCS"),sQuery(id+"F1.wireOp",EDGE,"E93.MirrorCS"),sQuery(id+"F1.wireOp",EDGE,"E94.MirrorCS"),sQuery(id+"F1.wireOp",EDGE,"E95.MirrorCS"),sQuery(id+"F1.wireOp",EDGE,"E96.MirrorCS"),sQuery(id+"F1.wireOp",EDGE,"E97.MirrorCS"),sQuery(id+"F1.wireOp",EDGE,"E99.MirrorCS"),sQuery(id+"F1.wireOp",EDGE,"E90.MirrorCS"),sQuery(id+"F1.wireOp",EDGE,"E100.MirrorCS"),sQuery(id+"F1.wireOp",EDGE,"E101"),sQuery(id+"F1.wireOp",EDGE,"E102"),sQuery(id+"F1.wireOp",EDGE,"E103"),sQuery(id+"F1.wireOp",EDGE,"E113"),sQuery(id+"F1.wireOp",EDGE,"E26.MirrorCS")])],"isStart":false});
            var sketch = newSketch(context, id + "F5", { "sketchPlane" : qUnion([Q0])});
            skLineSegment(sketch, "E296", {"start": v(0, 0) * mm, "end": v(0, 65.4) * mm, "construction": true});
            skLineSegment(sketch, "E297", {"start": v(0, 0) * mm, "end": v(57.14, 0) * mm, "construction": true});
            skLineSegment(sketch, "E298.bottom", {"start": v(65, 57.64) * mm, "end": v(-65, 57.64) * mm, "construction": true});
            skLineSegment(sketch, "E298.top", {"start": v(65, 153.64) * mm, "end": v(-65, 153.64) * mm, "construction": true});
            skLineSegment(sketch, "E298.left", {"start": v(65, 57.64) * mm, "end": v(65, 153.64) * mm, "construction": true});
            skLineSegment(sketch, "E298.right", {"start": v(-65, 57.64) * mm, "end": v(-65, 153.64) * mm, "construction": true});
            skPoint(sketch, "E298.middle", {"position": v(0, 101.74) * mm});
            skLineSegment(sketch, "E299", {"start": v(-59.07, 76.04) * mm, "end": v(59.38, 76.04) * mm, "construction": true});
            skCircle(sketch, "E300", {"center": v(47.3, 76.04) * mm, "radius": 1.75 * mm});
            skCircle(sketch, "E301.MirrorC", {"center": v(-47.3, 76.04) * mm, "radius": 1.75 * mm});
            skCircle(sketch, "E302", {"center": v(0, 88.34) * mm, "radius": 27.5 * mm});
            skLineSegment(sketch, "E303.bottom", {"start": v(32.8, -150.4) * mm, "end": v(-32.8, -150.4) * mm});
            skLineSegment(sketch, "E303.top", {"start": v(32.8, -84.8) * mm, "end": v(-32.8, -84.8) * mm});
            skLineSegment(sketch, "E303.left", {"start": v(32.8, -150.4) * mm, "end": v(32.8, -84.8) * mm});
            skLineSegment(sketch, "E303.right", {"start": v(-32.8, -150.4) * mm, "end": v(-32.8, -84.8) * mm});
            skPoint(sketch, "E303.middle", {"position": v(0, -112.04) * mm});
            skLineSegment(sketch, "E304", {"start": v(-96.42, 153.5) * mm, "end": v(-17.22, 153.5) * mm, "construction": true});
            skPoint(sketch, "E304.startSnap0", {"position": v(-85, 153.5) * mm});
            skLineSegment(sketch, "E305", {"start": v(-100.65, 36.04) * mm, "end": v(-43.04, 36.04) * mm, "construction": true});
            skLineSegment(sketch, "E306", {"start": v(-96.39, -84.8) * mm, "end": v(32.8, -84.8) * mm, "construction": true});
            skLineSegment(sketch, "E307.bottom", {"start": v(64.86, -60.1) * mm, "end": v(-65.14, -60.1) * mm, "construction": true});
            skLineSegment(sketch, "E307.top", {"start": v(64.86, 35.9) * mm, "end": v(-65.14, 35.9) * mm, "construction": true});
            skLineSegment(sketch, "E307.left", {"start": v(64.86, -60.1) * mm, "end": v(64.86, 35.9) * mm, "construction": true});
            skLineSegment(sketch, "E307.right", {"start": v(-65.14, -60.1) * mm, "end": v(-65.14, 35.9) * mm, "construction": true});
            skLineSegment(sketch, "E308", {"start": v(-59.21, -41.7) * mm, "end": v(59.24, -41.7) * mm, "construction": true});
            skCircle(sketch, "E309", {"center": v(47.16, -41.7) * mm, "radius": 1.75 * mm});
            skCircle(sketch, "E310.MirrorC", {"center": v(-47.44, -41.7) * mm, "radius": 1.75 * mm});
            skCircle(sketch, "E311", {"center": v(-0.14, -29.4) * mm, "radius": 27.5 * mm});
            skSolve(sketch);
        }
        {
            var Q0;
            Q0=makeQuery(id+"F5.imprint","IMPRINT",FACE,{"disambiguationData":[TD([[makeQuery(id+"F5.imprint","IMPRINT",EDGE,{"derivedFrom":sQuery(id+"F5.wireOp",EDGE,"E300")}),1.0]])]});
            var Q1;
            Q1=makeQuery(id+"F5.imprint","IMPRINT",FACE,{"disambiguationData":[TD([[makeQuery(id+"F5.imprint","IMPRINT",EDGE,{"derivedFrom":sQuery(id+"F5.wireOp",EDGE,"E301.MirrorC")}),-1.0]])]});
            var Q2;
            Q2=makeQuery(id+"F5.imprint","IMPRINT",FACE,{"disambiguationData":[TD([[makeQuery(id+"F5.imprint","IMPRINT",EDGE,{"derivedFrom":sQuery(id+"F5.wireOp",EDGE,"E302")}),1.0]])]});
            var Q3;
            Q3=makeQuery(id+"F5.imprint","IMPRINT",FACE,{"disambiguationData":[TD([[makeQuery(id+"F5.imprint","IMPRINT",EDGE,{"derivedFrom":sQuery(id+"F5.wireOp",EDGE,"E303.bottom")}),-1.0]])]});
            var Q4;
            Q4=makeQuery(id+"F5.imprint","IMPRINT",FACE,{"disambiguationData":[TD([[makeQuery(id+"F5.imprint","IMPRINT",EDGE,{"derivedFrom":sQuery(id+"F5.wireOp",EDGE,"E311")}),1.0]])]});
            var Q5;
            Q5=makeQuery(id+"F5.imprint","IMPRINT",FACE,{"disambiguationData":[TD([[makeQuery(id+"F5.imprint","IMPRINT",EDGE,{"derivedFrom":sQuery(id+"F5.wireOp",EDGE,"E310.MirrorC")}),-1.0]])]});
            var Q6;
            Q6=makeQuery(id+"F5.imprint","IMPRINT",FACE,{"disambiguationData":[TD([[makeQuery(id+"F5.imprint","IMPRINT",EDGE,{"derivedFrom":sQuery(id+"F5.wireOp",EDGE,"E309")}),1.0]])]});
            extrude(context, id + "F6", {"entities" : qUnion([Q0, Q1, Q2, Q3, Q4, Q5, Q6]), "operationType" : NewBodyOperationType.REMOVE, "endBound" : BoundingType.THROUGH_ALL, "oppositeDirection" : true, "depth" : 25 * mm, "offsetDistance" : 25 * mm});
        }
        {
            var Q0;
            Q0=makeQuery(id+"F4.opExtrude","CAP_FACE",FACE,{"disambiguationData":[OSD([sQuery(id+"F1.wireOp",EDGE,"E28.MirrorCS"),sQuery(id+"F1.wireOp",EDGE,"E29.MirrorCS"),sQuery(id+"F1.wireOp",EDGE,"E32.MirrorCS"),sQuery(id+"F1.wireOp",EDGE,"E31.MirrorCS"),sQuery(id+"F1.wireOp",EDGE,"E33.MirrorCS"),sQuery(id+"F1.wireOp",EDGE,"E34.MirrorCS"),sQuery(id+"F1.wireOp",EDGE,"E35.MirrorCS"),sQuery(id+"F1.wireOp",EDGE,"E36.MirrorCS"),sQuery(id+"F1.wireOp",EDGE,"E37.MirrorCS"),sQuery(id+"F1.wireOp",EDGE,"E38.MirrorCS"),sQuery(id+"F1.wireOp",EDGE,"E39.MirrorCS"),sQuery(id+"F1.wireOp",EDGE,"E40.MirrorCS"),sQuery(id+"F1.wireOp",EDGE,"E41.MirrorCS"),sQuery(id+"F1.wireOp",EDGE,"E42.MirrorCS"),sQuery(id+"F1.wireOp",EDGE,"E43.MirrorCS"),sQuery(id+"F1.wireOp",EDGE,"E44.MirrorCS"),sQuery(id+"F1.wireOp",EDGE,"E46.MirrorCS"),sQuery(id+"F1.wireOp",EDGE,"E48.MirrorCS"),sQuery(id+"F1.wireOp",EDGE,"E49.MirrorCS"),sQuery(id+"F1.wireOp",EDGE,"E50.MirrorCS"),sQuery(id+"F1.wireOp",EDGE,"E51.MirrorCS"),sQuery(id+"F1.wireOp",EDGE,"E52.MirrorCS"),sQuery(id+"F1.wireOp",EDGE,"E55.MirrorCS"),sQuery(id+"F1.wireOp",EDGE,"E57.MirrorCS"),sQuery(id+"F1.wireOp",EDGE,"E58.MirrorCS"),sQuery(id+"F1.wireOp",EDGE,"E59.MirrorCS"),sQuery(id+"F1.wireOp",EDGE,"E63.MirrorCS"),sQuery(id+"F1.wireOp",EDGE,"E65.MirrorCS"),sQuery(id+"F1.wireOp",EDGE,"E67.MirrorCS"),sQuery(id+"F1.wireOp",EDGE,"E69.MirrorCS"),sQuery(id+"F1.wireOp",EDGE,"E70.MirrorCS"),sQuery(id+"F1.wireOp",EDGE,"E71.MirrorCS"),sQuery(id+"F1.wireOp",EDGE,"E61.MirrorCS"),sQuery(id+"F1.wireOp",EDGE,"e8588eaa-9efa-4205-b61b-f90bf4415c170.MirrorCS"),sQuery(id+"F1.wireOp",EDGE,"36257738-82ba-4ba0-81fc-16082718a7c60.MirrorCS"),sQuery(id+"F1.wireOp",EDGE,"36257738-82ba-4ba0-81fc-16082718a7c61.MirrorCS"),sQuery(id+"F1.wireOp",EDGE,"36257738-82ba-4ba0-81fc-16082718a7c62.MirrorCS"),sQuery(id+"F1.wireOp",EDGE,"36257738-82ba-4ba0-81fc-16082718a7c63.MirrorCS"),sQuery(id+"F1.wireOp",EDGE,"36257738-82ba-4ba0-81fc-16082718a7c64.MirrorCS"),sQuery(id+"F1.wireOp",EDGE,"36257738-82ba-4ba0-81fc-16082718a7c65.MirrorCS"),sQuery(id+"F1.wireOp",EDGE,"36257738-82ba-4ba0-81fc-16082718a7c66.MirrorCS"),sQuery(id+"F1.wireOp",EDGE,"36257738-82ba-4ba0-81fc-16082718a7c67.MirrorCS"),sQuery(id+"F1.wireOp",EDGE,"36257738-82ba-4ba0-81fc-16082718a7c68.MirrorCS"),sQuery(id+"F1.wireOp",EDGE,"36257738-82ba-4ba0-81fc-16082718a7c69.MirrorCS"),sQuery(id+"F1.wireOp",EDGE,"36257738-82ba-4ba0-81fc-16082718a7c610.MirrorCS"),sQuery(id+"F1.wireOp",EDGE,"36257738-82ba-4ba0-81fc-16082718a7c613.MirrorCS"),sQuery(id+"F1.wireOp",EDGE,"36257738-82ba-4ba0-81fc-16082718a7c614.MirrorCS"),sQuery(id+"F1.wireOp",EDGE,"36257738-82ba-4ba0-81fc-16082718a7c615.MirrorCS"),sQuery(id+"F1.wireOp",EDGE,"36257738-82ba-4ba0-81fc-16082718a7c616.MirrorCS"),sQuery(id+"F1.wireOp",EDGE,"36257738-82ba-4ba0-81fc-16082718a7c617.MirrorCS"),sQuery(id+"F1.wireOp",EDGE,"36257738-82ba-4ba0-81fc-16082718a7c619.MirrorCS"),sQuery(id+"F1.wireOp",EDGE,"36257738-82ba-4ba0-81fc-16082718a7c620.MirrorCS"),sQuery(id+"F1.wireOp",EDGE,"36257738-82ba-4ba0-81fc-16082718a7c621.MirrorCS"),sQuery(id+"F1.wireOp",EDGE,"40372ffb-725b-4850-b457-b66fe95233732.MirrorCS"),sQuery(id+"F1.wireOp",EDGE,"40372ffb-725b-4850-b457-b66fe95233735.MirrorCS"),sQuery(id+"F1.wireOp",EDGE,"40372ffb-725b-4850-b457-b66fe95233736.MirrorCS"),sQuery(id+"F1.wireOp",EDGE,"40372ffb-725b-4850-b457-b66fe95233737.MirrorCS"),sQuery(id+"F1.wireOp",EDGE,"40372ffb-725b-4850-b457-b66fe95233738.MirrorCS"),sQuery(id+"F1.wireOp",EDGE,"40372ffb-725b-4850-b457-b66fe95233739.MirrorCS"),sQuery(id+"F1.wireOp",EDGE,"40372ffb-725b-4850-b457-b66fe952337310.MirrorCS"),sQuery(id+"F1.wireOp",EDGE,"40372ffb-725b-4850-b457-b66fe952337311.MirrorCS"),sQuery(id+"F1.wireOp",EDGE,"40372ffb-725b-4850-b457-b66fe952337312.MirrorCS"),sQuery(id+"F1.wireOp",EDGE,"40372ffb-725b-4850-b457-b66fe952337313.MirrorCS"),sQuery(id+"F1.wireOp",EDGE,"40372ffb-725b-4850-b457-b66fe952337314.MirrorCS"),sQuery(id+"F1.wireOp",EDGE,"40372ffb-725b-4850-b457-b66fe952337315.MirrorCS"),sQuery(id+"F1.wireOp",EDGE,"40372ffb-725b-4850-b457-b66fe952337316.MirrorCS"),sQuery(id+"F1.wireOp",EDGE,"E107"),sQuery(id+"F1.wireOp",EDGE,"E109"),sQuery(id+"F1.wireOp",EDGE,"c3fa9b5a-0544-4550-84fd-f6a7fe45fc7a"),sQuery(id+"F1.wireOp",EDGE,"E116"),sQuery(id+"F1.wireOp",EDGE,"E117"),sQuery(id+"F1.wireOp",EDGE,"E118"),sQuery(id+"F1.wireOp",EDGE,"E119"),sQuery(id+"F1.wireOp",EDGE,"E120"),sQuery(id+"F1.wireOp",EDGE,"E121"),sQuery(id+"F1.wireOp",EDGE,"E26.MirrorCS"),sQuery(id+"F1.wireOp",EDGE,"E108"),sQuery(id+"F1.wireOp",EDGE,"E126.MirrorCS"),sQuery(id+"F1.wireOp",EDGE,"E127.MirrorCS"),sQuery(id+"F1.wireOp",EDGE,"E128.MirrorCS"),sQuery(id+"F1.wireOp",EDGE,"E130.MirrorCS"),sQuery(id+"F1.wireOp",EDGE,"807e1db5-489a-46d0-ba22-59ed571ced100.MirrorCS"),sQuery(id+"F1.wireOp",EDGE,"b59b1dd1-65a5-44b6-8e0e-b5285ab880250.MirrorCS"),sQuery(id+"F1.wireOp",EDGE,"2090725a-ee73-494c-9470-00650aba7dc70.MirrorCS"),sQuery(id+"F1.wireOp",EDGE,"E129.MirrorCS"),sQuery(id+"F1.wireOp",EDGE,"be5c08f3-bc99-41fd-8c54-f4cd79b87091.trimOffspring"),sQuery(id+"F1.wireOp",EDGE,"E131"),sQuery(id+"F1.wireOp",EDGE,"E132"),sQuery(id+"F1.wireOp",EDGE,"E133"),sQuery(id+"F1.wireOp",EDGE,"E134"),sQuery(id+"F1.wireOp",EDGE,"E135"),sQuery(id+"F1.wireOp",EDGE,"E136"),sQuery(id+"F1.wireOp",EDGE,"E137"),sQuery(id+"F1.wireOp",EDGE,"E138"),sQuery(id+"F1.wireOp",EDGE,"E139"),sQuery(id+"F1.wireOp",EDGE,"E140"),sQuery(id+"F1.wireOp",EDGE,"E141"),sQuery(id+"F1.wireOp",EDGE,"E142"),sQuery(id+"F1.wireOp",EDGE,"E143"),sQuery(id+"F1.wireOp",EDGE,"E144"),sQuery(id+"F1.wireOp",EDGE,"E145"),sQuery(id+"F1.wireOp",EDGE,"E146"),sQuery(id+"F1.wireOp",EDGE,"E147"),sQuery(id+"F1.wireOp",EDGE,"E148"),sQuery(id+"F1.wireOp",EDGE,"E149"),sQuery(id+"F1.wireOp",EDGE,"E150"),sQuery(id+"F1.wireOp",EDGE,"E151"),sQuery(id+"F1.wireOp",EDGE,"E152"),sQuery(id+"F1.wireOp",EDGE,"E153"),sQuery(id+"F1.wireOp",EDGE,"E154"),sQuery(id+"F1.wireOp",EDGE,"E155"),sQuery(id+"F1.wireOp",EDGE,"E156"),sQuery(id+"F1.wireOp",EDGE,"E157"),sQuery(id+"F1.wireOp",EDGE,"E158"),sQuery(id+"F1.wireOp",EDGE,"E159"),sQuery(id+"F1.wireOp",EDGE,"E160"),sQuery(id+"F1.wireOp",EDGE,"E161"),sQuery(id+"F1.wireOp",EDGE,"E162"),sQuery(id+"F1.wireOp",EDGE,"E163"),sQuery(id+"F1.wireOp",EDGE,"E164"),sQuery(id+"F1.wireOp",EDGE,"E165"),sQuery(id+"F1.wireOp",EDGE,"E166"),sQuery(id+"F1.wireOp",EDGE,"E167"),sQuery(id+"F1.wireOp",EDGE,"E168"),sQuery(id+"F1.wireOp",EDGE,"E169"),sQuery(id+"F1.wireOp",EDGE,"E170"),sQuery(id+"F1.wireOp",EDGE,"E171"),sQuery(id+"F1.wireOp",EDGE,"E172"),sQuery(id+"F1.wireOp",EDGE,"E173"),sQuery(id+"F1.wireOp",EDGE,"E194"),sQuery(id+"F1.wireOp",EDGE,"E195"),sQuery(id+"F1.wireOp",EDGE,"E196.trimOffspring"),sQuery(id+"F1.wireOp",EDGE,"E197.trimOffspring"),sQuery(id+"F1.wireOp",EDGE,"E198"),sQuery(id+"F1.wireOp",EDGE,"E199"),sQuery(id+"F1.wireOp",EDGE,"E200.trimOffspring"),sQuery(id+"F1.wireOp",EDGE,"E201.trimOffspring"),sQuery(id+"F1.wireOp",EDGE,"E202"),sQuery(id+"F1.wireOp",EDGE,"E203"),sQuery(id+"F1.wireOp",EDGE,"E204"),sQuery(id+"F1.wireOp",EDGE,"E205"),sQuery(id+"F1.wireOp",EDGE,"E206.trimOffspring"),sQuery(id+"F1.wireOp",EDGE,"E207.trimOffspring"),sQuery(id+"F1.wireOp",EDGE,"E208.trimOffspring"),sQuery(id+"F1.wireOp",EDGE,"E209.trimOffspring"),sQuery(id+"F1.wireOp",EDGE,"E210")])],"isStart":false});
            var sketch = newSketch(context, id + "F7", { "sketchPlane" : qUnion([Q0])});
            skCircle(sketch, "E312", {"center": v(120.48, 20) * mm, "radius": 2.5 * mm});
            skCircle(sketch, "E313.1.0", {"center": v(130.55, 17.61) * mm, "radius": 2.5 * mm});
            skCircle(sketch, "E313.2.0", {"center": v(138.09, 10.51) * mm, "radius": 2.5 * mm});
            skCircle(sketch, "E313.3.0", {"center": v(141.06, 0.6) * mm, "radius": 2.5 * mm});
            skCircle(sketch, "E313.4.0", {"center": v(138.68, -9.48) * mm, "radius": 2.5 * mm});
            skCircle(sketch, "E313.5.0", {"center": v(131.58, -17.02) * mm, "radius": 2.5 * mm});
            skCircle(sketch, "E313.6.0", {"center": v(121.67, -20) * mm, "radius": 2.5 * mm});
            skCircle(sketch, "E313.7.0", {"center": v(111.6, -17.61) * mm, "radius": 2.5 * mm});
            skCircle(sketch, "E313.8.0", {"center": v(104.06, -10.51) * mm, "radius": 2.5 * mm});
            skCircle(sketch, "E313.9.0", {"center": v(101.08, -0.6) * mm, "radius": 2.5 * mm});
            skCircle(sketch, "E313.10.0", {"center": v(103.46, 9.48) * mm, "radius": 2.5 * mm});
            skCircle(sketch, "E313.11.0", {"center": v(110.56, 17.02) * mm, "radius": 2.5 * mm});
            skPoint(sketch, "E313.center", {"position": v(121.07, 0) * mm});
            skLineSegment(sketch, "E313.anchor1", {"start": v(121.07, 0) * mm, "end": v(120.48, 20) * mm, "construction": true});
            skLineSegment(sketch, "E313.anchor2", {"start": v(121.07, 0) * mm, "end": v(110.56, 17.02) * mm, "construction": true});
            skCircle(sketch, "E314", {"center": v(124.34, 13.43) * mm, "radius": 2.25 * mm});
            skCircle(sketch, "E315.1.0", {"center": v(117.2, 13.26) * mm, "radius": 2.25 * mm});
            skCircle(sketch, "E315.2.0", {"center": v(111.08, 9.55) * mm, "radius": 2.25 * mm});
            skCircle(sketch, "E315.3.0", {"center": v(107.64, 3.27) * mm, "radius": 2.25 * mm});
            skCircle(sketch, "E315.4.0", {"center": v(107.8, -3.88) * mm, "radius": 2.25 * mm});
            skCircle(sketch, "E315.5.0", {"center": v(111.53, -10) * mm, "radius": 2.25 * mm});
            skCircle(sketch, "E315.6.0", {"center": v(117.8, -13.43) * mm, "radius": 2.25 * mm});
            skCircle(sketch, "E315.7.0", {"center": v(124.95, -13.26) * mm, "radius": 2.25 * mm});
            skCircle(sketch, "E315.8.0", {"center": v(131.07, -9.55) * mm, "radius": 2.25 * mm});
            skCircle(sketch, "E315.9.0", {"center": v(134.5, -3.27) * mm, "radius": 2.25 * mm});
            skCircle(sketch, "E315.10.0", {"center": v(134.34, 3.88) * mm, "radius": 2.25 * mm});
            skCircle(sketch, "E315.11.0", {"center": v(130.62, 10) * mm, "radius": 2.25 * mm});
            skCircle(sketch, "E316", {"center": v(123.88, 5.47) * mm, "radius": 1.54 * mm});
            skCircle(sketch, "E317.1.0", {"center": v(126.74, 2.39) * mm, "radius": 1.54 * mm});
            skCircle(sketch, "E317.2.0", {"center": v(126.95, -1.82) * mm, "radius": 1.54 * mm});
            skCircle(sketch, "E317.3.0", {"center": v(124.4, -5.17) * mm, "radius": 1.54 * mm});
            skCircle(sketch, "E317.4.0", {"center": v(120.3, -6.1) * mm, "radius": 1.54 * mm});
            skCircle(sketch, "E317.5.0", {"center": v(116.56, -4.18) * mm, "radius": 1.54 * mm});
            skCircle(sketch, "E317.6.0", {"center": v(114.93, -0.3) * mm, "radius": 1.54 * mm});
            skCircle(sketch, "E317.7.0", {"center": v(116.17, 3.72) * mm, "radius": 1.54 * mm});
            skCircle(sketch, "E317.8.0", {"center": v(119.7, 6) * mm, "radius": 1.54 * mm});
            skLineSegment(sketch, "E317.anchor1", {"start": v(121.07, 0) * mm, "end": v(123.88, 5.47) * mm, "construction": true});
            skLineSegment(sketch, "E317.anchor2", {"start": v(121.07, 0) * mm, "end": v(119.7, 6) * mm, "construction": true});
            skCircle(sketch, "E318", {"center": v(121.07, 2.74) * mm, "radius": 1.25 * mm});
            skPoint(sketch, "E318.centerSnap0", {"position": v(122.48, 2.74) * mm});
            skCircle(sketch, "E319.1.0", {"center": v(118.7, -1.37) * mm, "radius": 1.25 * mm});
            skCircle(sketch, "E319.2.0", {"center": v(123.44, -1.37) * mm, "radius": 1.25 * mm});
            skSolve(sketch);
        }
        {
            var Q0;
            Q0=makeQuery(id+"F7.imprint","IMPRINT",FACE,{"disambiguationData":[TD([[makeQuery(id+"F7.imprint","IMPRINT",EDGE,{"derivedFrom":sQuery(id+"F7.wireOp",EDGE,"E313.3.0")}),1.0]])]});
            var Q1;
            Q1=makeQuery(id+"F7.imprint","IMPRINT",FACE,{"disambiguationData":[TD([[makeQuery(id+"F7.imprint","IMPRINT",EDGE,{"derivedFrom":sQuery(id+"F7.wireOp",EDGE,"E313.2.0")}),1.0]])]});
            var Q2;
            Q2=makeQuery(id+"F7.imprint","IMPRINT",FACE,{"disambiguationData":[TD([[makeQuery(id+"F7.imprint","IMPRINT",EDGE,{"derivedFrom":sQuery(id+"F7.wireOp",EDGE,"E315.10.0")}),1.0]])]});
            var Q3;
            Q3=makeQuery(id+"F7.imprint","IMPRINT",FACE,{"disambiguationData":[TD([[makeQuery(id+"F7.imprint","IMPRINT",EDGE,{"derivedFrom":sQuery(id+"F7.wireOp",EDGE,"E315.11.0")}),1.0]])]});
            var Q4;
            Q4=makeQuery(id+"F7.imprint","IMPRINT",FACE,{"disambiguationData":[TD([[makeQuery(id+"F7.imprint","IMPRINT",EDGE,{"derivedFrom":sQuery(id+"F7.wireOp",EDGE,"E313.1.0")}),1.0]])]});
            var Q5;
            Q5=makeQuery(id+"F7.imprint","IMPRINT",FACE,{"disambiguationData":[TD([[makeQuery(id+"F7.imprint","IMPRINT",EDGE,{"derivedFrom":sQuery(id+"F7.wireOp",EDGE,"E314")}),1.0]])]});
            var Q6;
            Q6=makeQuery(id+"F7.imprint","IMPRINT",FACE,{"disambiguationData":[TD([[makeQuery(id+"F7.imprint","IMPRINT",EDGE,{"derivedFrom":sQuery(id+"F7.wireOp",EDGE,"E315.1.0")}),1.0]])]});
            var Q7;
            Q7=makeQuery(id+"F7.imprint","IMPRINT",FACE,{"disambiguationData":[TD([[makeQuery(id+"F7.imprint","IMPRINT",EDGE,{"derivedFrom":sQuery(id+"F7.wireOp",EDGE,"E315.2.0")}),1.0]])]});
            var Q8;
            Q8=makeQuery(id+"F7.imprint","IMPRINT",FACE,{"disambiguationData":[TD([[makeQuery(id+"F7.imprint","IMPRINT",EDGE,{"derivedFrom":sQuery(id+"F7.wireOp",EDGE,"E313.10.0")}),1.0]])]});
            var Q9;
            Q9=makeQuery(id+"F7.imprint","IMPRINT",FACE,{"disambiguationData":[TD([[makeQuery(id+"F7.imprint","IMPRINT",EDGE,{"derivedFrom":sQuery(id+"F7.wireOp",EDGE,"E313.9.0")}),1.0]])]});
            var Q10;
            Q10=makeQuery(id+"F7.imprint","IMPRINT",FACE,{"disambiguationData":[TD([[makeQuery(id+"F7.imprint","IMPRINT",EDGE,{"derivedFrom":sQuery(id+"F7.wireOp",EDGE,"E315.4.0")}),1.0]])]});
            var Q11;
            Q11=makeQuery(id+"F7.imprint","IMPRINT",FACE,{"disambiguationData":[TD([[makeQuery(id+"F7.imprint","IMPRINT",EDGE,{"derivedFrom":sQuery(id+"F7.wireOp",EDGE,"E313.8.0")}),1.0]])]});
            var Q12;
            Q12=makeQuery(id+"F7.imprint","IMPRINT",FACE,{"disambiguationData":[TD([[makeQuery(id+"F7.imprint","IMPRINT",EDGE,{"derivedFrom":sQuery(id+"F7.wireOp",EDGE,"E315.5.0")}),1.0]])]});
            var Q13;
            Q13=makeQuery(id+"F7.imprint","IMPRINT",FACE,{"disambiguationData":[TD([[makeQuery(id+"F7.imprint","IMPRINT",EDGE,{"derivedFrom":sQuery(id+"F7.wireOp",EDGE,"E315.3.0")}),1.0]])]});
            var Q14;
            Q14=makeQuery(id+"F7.imprint","IMPRINT",FACE,{"disambiguationData":[TD([[makeQuery(id+"F7.imprint","IMPRINT",EDGE,{"derivedFrom":sQuery(id+"F7.wireOp",EDGE,"E313.7.0")}),1.0]])]});
            var Q15;
            Q15=makeQuery(id+"F7.imprint","IMPRINT",FACE,{"disambiguationData":[TD([[makeQuery(id+"F7.imprint","IMPRINT",EDGE,{"derivedFrom":sQuery(id+"F7.wireOp",EDGE,"E315.6.0")}),1.0]])]});
            var Q16;
            Q16=makeQuery(id+"F7.imprint","IMPRINT",FACE,{"disambiguationData":[TD([[makeQuery(id+"F7.imprint","IMPRINT",EDGE,{"derivedFrom":sQuery(id+"F7.wireOp",EDGE,"E315.7.0")}),1.0]])]});
            var Q17;
            Q17=makeQuery(id+"F7.imprint","IMPRINT",FACE,{"disambiguationData":[TD([[makeQuery(id+"F7.imprint","IMPRINT",EDGE,{"derivedFrom":sQuery(id+"F7.wireOp",EDGE,"E313.6.0")}),1.0]])]});
            var Q18;
            Q18=makeQuery(id+"F7.imprint","IMPRINT",FACE,{"disambiguationData":[TD([[makeQuery(id+"F7.imprint","IMPRINT",EDGE,{"derivedFrom":sQuery(id+"F7.wireOp",EDGE,"E313.5.0")}),1.0]])]});
            var Q19;
            Q19=makeQuery(id+"F7.imprint","IMPRINT",FACE,{"disambiguationData":[TD([[makeQuery(id+"F7.imprint","IMPRINT",EDGE,{"derivedFrom":sQuery(id+"F7.wireOp",EDGE,"E315.8.0")}),1.0]])]});
            var Q20;
            Q20=makeQuery(id+"F7.imprint","IMPRINT",FACE,{"disambiguationData":[TD([[makeQuery(id+"F7.imprint","IMPRINT",EDGE,{"derivedFrom":sQuery(id+"F7.wireOp",EDGE,"E315.9.0")}),1.0]])]});
            var Q21;
            Q21=makeQuery(id+"F7.imprint","IMPRINT",FACE,{"disambiguationData":[TD([[makeQuery(id+"F7.imprint","IMPRINT",EDGE,{"derivedFrom":sQuery(id+"F7.wireOp",EDGE,"E313.4.0")}),1.0]])]});
            var Q22;
            Q22=makeQuery(id+"F7.imprint","IMPRINT",FACE,{"disambiguationData":[TD([[makeQuery(id+"F7.imprint","IMPRINT",EDGE,{"derivedFrom":sQuery(id+"F7.wireOp",EDGE,"E318")}),1.0]])]});
            var Q23;
            Q23=makeQuery(id+"F7.imprint","IMPRINT",FACE,{"disambiguationData":[TD([[makeQuery(id+"F7.imprint","IMPRINT",EDGE,{"derivedFrom":sQuery(id+"F7.wireOp",EDGE,"E319.1.0")}),1.0]])]});
            var Q24;
            Q24=makeQuery(id+"F7.imprint","IMPRINT",FACE,{"disambiguationData":[TD([[makeQuery(id+"F7.imprint","IMPRINT",EDGE,{"derivedFrom":sQuery(id+"F7.wireOp",EDGE,"E317.4.0")}),1.0]])]});
            var Q25;
            Q25=makeQuery(id+"F7.imprint","IMPRINT",FACE,{"disambiguationData":[TD([[makeQuery(id+"F7.imprint","IMPRINT",EDGE,{"derivedFrom":sQuery(id+"F7.wireOp",EDGE,"E317.5.0")}),1.0]])]});
            var Q26;
            Q26=makeQuery(id+"F7.imprint","IMPRINT",FACE,{"disambiguationData":[TD([[makeQuery(id+"F7.imprint","IMPRINT",EDGE,{"derivedFrom":sQuery(id+"F7.wireOp",EDGE,"E317.6.0")}),1.0]])]});
            var Q27;
            Q27=makeQuery(id+"F7.imprint","IMPRINT",FACE,{"disambiguationData":[TD([[makeQuery(id+"F7.imprint","IMPRINT",EDGE,{"derivedFrom":sQuery(id+"F7.wireOp",EDGE,"E317.7.0")}),1.0]])]});
            var Q28;
            Q28=makeQuery(id+"F7.imprint","IMPRINT",FACE,{"disambiguationData":[TD([[makeQuery(id+"F7.imprint","IMPRINT",EDGE,{"derivedFrom":sQuery(id+"F7.wireOp",EDGE,"E317.8.0")}),1.0]])]});
            var Q29;
            Q29=makeQuery(id+"F7.imprint","IMPRINT",FACE,{"disambiguationData":[TD([[makeQuery(id+"F7.imprint","IMPRINT",EDGE,{"derivedFrom":sQuery(id+"F7.wireOp",EDGE,"E316")}),1.0]])]});
            var Q30;
            Q30=makeQuery(id+"F7.imprint","IMPRINT",FACE,{"disambiguationData":[TD([[makeQuery(id+"F7.imprint","IMPRINT",EDGE,{"derivedFrom":sQuery(id+"F7.wireOp",EDGE,"E317.1.0")}),1.0]])]});
            var Q31;
            Q31=makeQuery(id+"F7.imprint","IMPRINT",FACE,{"disambiguationData":[TD([[makeQuery(id+"F7.imprint","IMPRINT",EDGE,{"derivedFrom":sQuery(id+"F7.wireOp",EDGE,"E317.2.0")}),1.0]])]});
            var Q32;
            Q32=makeQuery(id+"F7.imprint","IMPRINT",FACE,{"disambiguationData":[TD([[makeQuery(id+"F7.imprint","IMPRINT",EDGE,{"derivedFrom":sQuery(id+"F7.wireOp",EDGE,"E317.3.0")}),1.0]])]});
            var Q33;
            Q33=makeQuery(id+"F7.imprint","IMPRINT",FACE,{"disambiguationData":[TD([[makeQuery(id+"F7.imprint","IMPRINT",EDGE,{"derivedFrom":sQuery(id+"F7.wireOp",EDGE,"E313.11.0")}),1.0]])]});
            var Q34;
            Q34=makeQuery(id+"F7.imprint","IMPRINT",FACE,{"disambiguationData":[TD([[makeQuery(id+"F7.imprint","IMPRINT",EDGE,{"derivedFrom":sQuery(id+"F7.wireOp",EDGE,"E312")}),1.0]])]});
            var Q35;
            Q35=makeQuery(id+"F7.imprint","IMPRINT",FACE,{"disambiguationData":[TD([[makeQuery(id+"F7.imprint","IMPRINT",EDGE,{"derivedFrom":sQuery(id+"F7.wireOp",EDGE,"E319.2.0")}),1.0]])]});
            var Q36;
            Q36=makeQuery(id+"F7.imprint","IMPRINT",FACE,{"disambiguationData":[TD([[makeQuery(id+"F7.imprint","IMPRINT",EDGE,{"derivedFrom":sQuery(id+"F7.wireOp",EDGE,"E319.2.0")}),1.0]])]});
            extrude(context, id + "F8", {"entities" : qUnion([Q0, Q1, Q2, Q3, Q4, Q5, Q6, Q7, Q8, Q9, Q10, Q11, Q12, Q13, Q14, Q15, Q16, Q17, Q18, Q19, Q20, Q21, Q22, Q23, Q24, Q25, Q26, Q27, Q28, Q29, Q30, Q31, Q32, Q33, Q34, Q35, Q36]), "operationType" : NewBodyOperationType.REMOVE, "endBound" : BoundingType.THROUGH_ALL, "oppositeDirection" : true, "depth" : 25 * mm, "offsetDistance" : 25 * mm});
        }
    });
